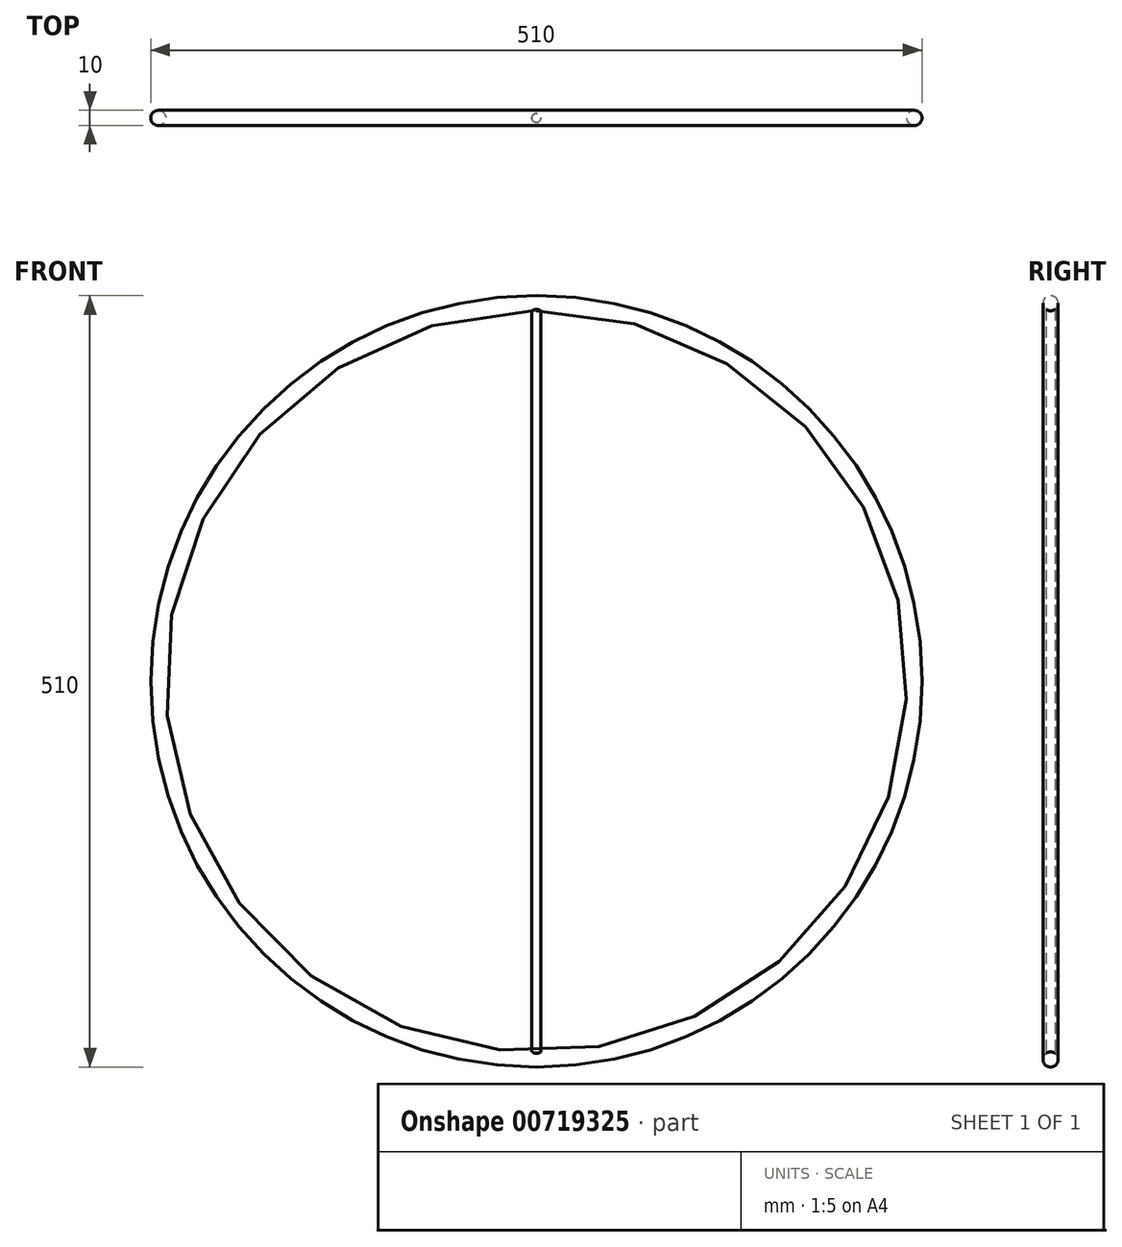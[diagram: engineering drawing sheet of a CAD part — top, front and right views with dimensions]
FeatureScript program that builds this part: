
annotation { "Feature Type Name" : "Feature", "Feature Type Description" : "" }
export const myFeature = defineFeature(function(context is Context, id is Id, definition is map)
    precondition{}
    {
        {
            var Q0;
            Q0=qCreatedBy(makeId("Top.planeOp"),FACE);
            var sketch = newSketch(context, id + "F0", { "sketchPlane" : qUnion([Q0])});
            skCircle(sketch, "E0", {"center": v(250, 0) * mm, "radius": 5 * mm});
            skLineSegment(sketch, "E1", {"start": v(0, 14.48) * mm, "end": v(0, -16.44) * mm});
            skCircle(sketch, "E2", {"center": v(0, 0) * mm, "radius": 1.66 * mm});
            skSolve(sketch);
        }
        {
            var Q0;
            Q0=makeQuery(id+"F0.imprint","IMPRINT",FACE,{"disambiguationData":[TD([[makeQuery(id+"F0.imprint","IMPRINT",EDGE,{"derivedFrom":sQuery(id+"F0.wireOp",EDGE,"E0")}),1.0]])]});
            var Q1;
            Q1=sQuery(id+"F0.wireOp",EDGE,"E1");
            revolve(context, id + "F1", {"surfaceOperationType" : NewSurfaceOperationType.NEW, "entities" : qUnion([Q0]), "axis" : qUnion([Q1]), "revolveType" : RevolveType.FULL});
        }
        {
            var Q0;
            Q0=qCreatedBy(makeId("Top.planeOp"),FACE);
            var sketch = newSketch(context, id + "F2", { "sketchPlane" : qUnion([Q0])});
            skCircle(sketch, "E3", {"center": v(0, 0) * mm, "radius": 3 * mm});
            skSolve(sketch);
        }
        {
            var Q0;
            Q0=makeQuery(id+"F2.imprint","IMPRINT",FACE,{"disambiguationData":[TD([[makeQuery(id+"F2.imprint","IMPRINT",EDGE,{"derivedFrom":sQuery(id+"F2.wireOp",EDGE,"E3")}),1.0]])]});
            extrude(context, id + "F3", {"entities" : qUnion([Q0]), "endBound" : BoundingType.UP_TO_NEXT, "depth" : 25 * mm, "offsetDistance" : 25 * mm, "hasSecondDirection" : true, "secondDirectionBound" : SecondDirectionBoundingType.UP_TO_NEXT, "secondDirectionOppositeDirection" : true, "secondDirectionDepth" : 25 * mm});
        }
    });
